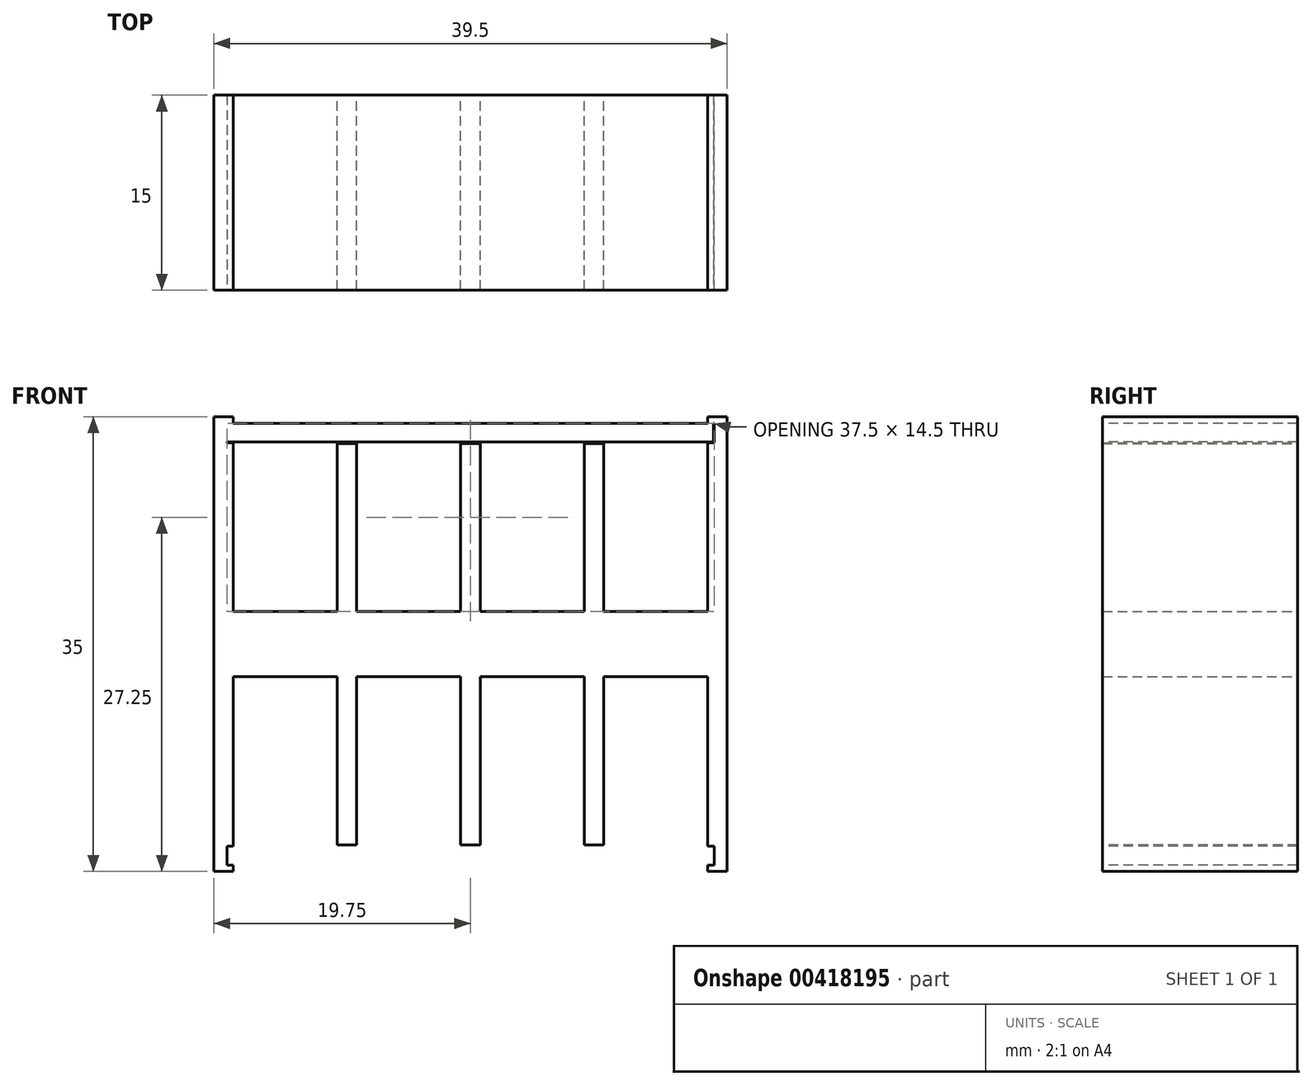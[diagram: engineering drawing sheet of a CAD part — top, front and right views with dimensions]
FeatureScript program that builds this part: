
annotation { "Feature Type Name" : "Feature", "Feature Type Description" : "" }
export const myFeature = defineFeature(function(context is Context, id is Id, definition is map)
    precondition{}
    {
        {
            var Q0;
            Q0=qCreatedBy(makeId("Top.planeOp"),FACE);
            var sketch = newSketch(context, id + "F0", { "sketchPlane" : qUnion([Q0])});
            skLineSegment(sketch, "E0.bottom", {"start": v(19.75, -7.5) * mm, "end": v(-19.75, -7.5) * mm});
            skLineSegment(sketch, "E0.top", {"start": v(19.75, 7.5) * mm, "end": v(-19.75, 7.5) * mm});
            skLineSegment(sketch, "E0.left", {"start": v(19.75, -7.5) * mm, "end": v(19.75, 7.5) * mm});
            skLineSegment(sketch, "E0.right", {"start": v(-19.75, -7.5) * mm, "end": v(-19.75, 7.5) * mm});
            skPoint(sketch, "E0.middle", {"position": v(0, 0) * mm});
            skSolve(sketch);
        }
        {
            var Q0;
            Q0=makeQuery(id+"F0.imprint","IMPRINT",FACE,{"disambiguationData":[TD([[makeQuery(id+"F0.imprint","IMPRINT",EDGE,{"derivedFrom":sQuery(id+"F0.wireOp",EDGE,"E0.bottom")}),-1.0]])]});
            extrude(context, id + "F1", {"entities" : qUnion([Q0]), "depth" : 5 * mm});
        }
        {
            var Q0;
            Q0=makeQuery(id+"F1.opExtrude","CAP_FACE",FACE,{"disambiguationData":[OSD([sQuery(id+"F0.wireOp",EDGE,"E0.bottom"),sQuery(id+"F0.wireOp",EDGE,"E0.top"),sQuery(id+"F0.wireOp",EDGE,"E0.left"),sQuery(id+"F0.wireOp",EDGE,"E0.right")])],"isStart":false});
            var sketch = newSketch(context, id + "F2", { "sketchPlane" : qUnion([Q0])});
            skLineSegment(sketch, "E1.bottom", {"start": v(-19.75, 7.5) * mm, "end": v(-18.25, 7.5) * mm});
            skLineSegment(sketch, "E1.top", {"start": v(-19.75, -7.5) * mm, "end": v(-18.25, -7.5) * mm});
            skLineSegment(sketch, "E1.left", {"start": v(-19.75, 7.5) * mm, "end": v(-19.75, -7.5) * mm});
            skLineSegment(sketch, "E1.right", {"start": v(-18.25, 7.5) * mm, "end": v(-18.25, -7.5) * mm});
            skLineSegment(sketch, "E2.bottom", {"start": v(19.75, 7.5) * mm, "end": v(18.25, 7.5) * mm});
            skLineSegment(sketch, "E2.top", {"start": v(19.75, -7.5) * mm, "end": v(18.25, -7.5) * mm});
            skLineSegment(sketch, "E2.left", {"start": v(19.75, 7.5) * mm, "end": v(19.75, -7.5) * mm});
            skLineSegment(sketch, "E2.right", {"start": v(18.25, 7.5) * mm, "end": v(18.25, -7.5) * mm});
            skLineSegment(sketch, "E3.bottom", {"start": v(0.75, -7.5) * mm, "end": v(-0.75, -7.5) * mm});
            skLineSegment(sketch, "E3.top", {"start": v(0.75, 7.5) * mm, "end": v(-0.75, 7.5) * mm});
            skLineSegment(sketch, "E3.left", {"start": v(0.75, -7.5) * mm, "end": v(0.75, 7.5) * mm});
            skLineSegment(sketch, "E3.right", {"start": v(-0.75, -7.5) * mm, "end": v(-0.75, 7.5) * mm});
            skPoint(sketch, "E3.middle", {"position": v(0, 0) * mm});
            skLineSegment(sketch, "E4.bottom", {"start": v(-18.25, 7.5) * mm, "end": v(-15.25, 7.5) * mm});
            skLineSegment(sketch, "E4.top", {"start": v(-18.25, -7.5) * mm, "end": v(-15.25, -7.5) * mm});
            skLineSegment(sketch, "E4.right", {"start": v(-15.25, 7.5) * mm, "end": v(-15.25, -7.5) * mm});
            skLineSegment(sketch, "E5.bottom", {"start": v(-0.75, 7.5) * mm, "end": v(-3.75, 7.5) * mm});
            skLineSegment(sketch, "E5.top", {"start": v(-0.75, -7.5) * mm, "end": v(-3.75, -7.5) * mm});
            skLineSegment(sketch, "E5.left", {"start": v(-0.75, 7.5) * mm, "end": v(-0.75, -7.5) * mm});
            skLineSegment(sketch, "E5.right", {"start": v(-3.75, 7.5) * mm, "end": v(-3.75, -7.5) * mm});
            skLineSegment(sketch, "E6.bottom", {"start": v(0.75, 7.5) * mm, "end": v(3.75, 7.5) * mm});
            skLineSegment(sketch, "E6.top", {"start": v(0.75, -7.5) * mm, "end": v(3.75, -7.5) * mm});
            skLineSegment(sketch, "E6.left", {"start": v(0.75, 7.5) * mm, "end": v(0.75, -7.5) * mm});
            skLineSegment(sketch, "E6.right", {"start": v(3.75, 7.5) * mm, "end": v(3.75, -7.5) * mm});
            skLineSegment(sketch, "E7.bottom", {"start": v(18.25, -7.5) * mm, "end": v(15.25, -7.5) * mm});
            skLineSegment(sketch, "E7.top", {"start": v(18.25, 7.5) * mm, "end": v(15.25, 7.5) * mm});
            skLineSegment(sketch, "E7.left", {"start": v(18.25, -7.5) * mm, "end": v(18.25, 7.5) * mm});
            skLineSegment(sketch, "E7.right", {"start": v(15.25, -7.5) * mm, "end": v(15.25, 7.5) * mm});
            skLineSegment(sketch, "E8.bottom", {"start": v(-15.25, 7.5) * mm, "end": v(-13.25, 7.5) * mm});
            skLineSegment(sketch, "E8.top", {"start": v(-15.25, -7.5) * mm, "end": v(-13.25, -7.5) * mm});
            skLineSegment(sketch, "E8.right", {"start": v(-13.25, 7.5) * mm, "end": v(-13.25, -7.5) * mm});
            skLineSegment(sketch, "E9.bottom", {"start": v(-3.75, -7.5) * mm, "end": v(-5.75, -7.5) * mm});
            skLineSegment(sketch, "E9.top", {"start": v(-3.75, 7.5) * mm, "end": v(-5.75, 7.5) * mm});
            skLineSegment(sketch, "E9.left", {"start": v(-3.75, -7.5) * mm, "end": v(-3.75, 7.5) * mm});
            skLineSegment(sketch, "E9.right", {"start": v(-5.75, -7.5) * mm, "end": v(-5.75, 7.5) * mm});
            skLineSegment(sketch, "E10.bottom", {"start": v(3.75, 7.5) * mm, "end": v(5.75, 7.5) * mm});
            skLineSegment(sketch, "E10.top", {"start": v(3.75, -7.5) * mm, "end": v(5.75, -7.5) * mm});
            skLineSegment(sketch, "E10.right", {"start": v(5.75, 7.5) * mm, "end": v(5.75, -7.5) * mm});
            skLineSegment(sketch, "E11.bottom", {"start": v(15.25, -7.5) * mm, "end": v(13.25, -7.5) * mm});
            skLineSegment(sketch, "E11.top", {"start": v(15.25, 7.5) * mm, "end": v(13.25, 7.5) * mm});
            skLineSegment(sketch, "E11.right", {"start": v(13.25, -7.5) * mm, "end": v(13.25, 7.5) * mm});
            skLineSegment(sketch, "E12.bottom", {"start": v(-13.25, 7.5) * mm, "end": v(-10.25, 7.5) * mm});
            skLineSegment(sketch, "E12.top", {"start": v(-13.25, -7.5) * mm, "end": v(-10.25, -7.5) * mm});
            skLineSegment(sketch, "E12.right", {"start": v(-10.25, 7.5) * mm, "end": v(-10.25, -7.5) * mm});
            skLineSegment(sketch, "E13.bottom", {"start": v(-5.75, -7.5) * mm, "end": v(-8.75, -7.5) * mm});
            skLineSegment(sketch, "E13.top", {"start": v(-5.75, 7.5) * mm, "end": v(-8.75, 7.5) * mm});
            skLineSegment(sketch, "E13.right", {"start": v(-8.75, -7.5) * mm, "end": v(-8.75, 7.5) * mm});
            skLineSegment(sketch, "E14.bottom", {"start": v(5.75, 7.5) * mm, "end": v(8.75, 7.5) * mm});
            skLineSegment(sketch, "E14.top", {"start": v(5.75, -7.5) * mm, "end": v(8.75, -7.5) * mm});
            skLineSegment(sketch, "E14.right", {"start": v(8.75, 7.5) * mm, "end": v(8.75, -7.5) * mm});
            skLineSegment(sketch, "E15.bottom", {"start": v(13.25, 7.5) * mm, "end": v(10.25, 7.5) * mm});
            skLineSegment(sketch, "E15.top", {"start": v(13.25, -7.5) * mm, "end": v(10.25, -7.5) * mm});
            skLineSegment(sketch, "E15.left", {"start": v(13.25, 7.5) * mm, "end": v(13.25, -7.5) * mm});
            skLineSegment(sketch, "E15.right", {"start": v(10.25, 7.5) * mm, "end": v(10.25, -7.5) * mm});
            skLineSegment(sketch, "E16.bottom", {"start": v(-10.25, -7.5) * mm, "end": v(-8.75, -7.5) * mm});
            skLineSegment(sketch, "E16.top", {"start": v(-10.25, 7.5) * mm, "end": v(-8.75, 7.5) * mm});
            skLineSegment(sketch, "E16.left", {"start": v(-10.25, -7.5) * mm, "end": v(-10.25, 7.5) * mm});
            skLineSegment(sketch, "E17.bottom", {"start": v(8.75, 7.5) * mm, "end": v(10.25, 7.5) * mm});
            skLineSegment(sketch, "E17.top", {"start": v(8.75, -7.5) * mm, "end": v(10.25, -7.5) * mm});
            skLineSegment(sketch, "E18", {"start": v(13.25, 0) * mm, "end": v(15.25, 0) * mm});
            skCircle(sketch, "E19", {"center": v(-14.25, 0) * mm, "radius": 1 * mm});
            skCircle(sketch, "E20", {"center": v(-4.75, 0) * mm, "radius": 1 * mm});
            skCircle(sketch, "E21", {"center": v(4.75, 0) * mm, "radius": 1 * mm});
            skCircle(sketch, "E22", {"center": v(14.25, 0) * mm, "radius": 1 * mm});
            skSolve(sketch);
        }
        {
            var Q0;
            Q0=makeQuery(id+"F2.imprint","IMPRINT",FACE,{"disambiguationData":[TD([[makeQuery(id+"F2.imprint","IMPRINT",EDGE,{"derivedFrom":sQuery(id+"F2.wireOp",EDGE,"E1.bottom")}),1.0]])]});
            var Q1;
            Q1=makeQuery(id+"F2.imprint","IMPRINT",FACE,{"disambiguationData":[TD([[makeQuery(id+"F2.imprint","IMPRINT",EDGE,{"derivedFrom":sQuery(id+"F2.wireOp",EDGE,"E16.bottom")}),-1.0]])]});
            var Q2;
            Q2=makeQuery(id+"F2.imprint","IMPRINT",FACE,{"disambiguationData":[TD([[makeQuery(id+"F2.imprint","IMPRINT",EDGE,{"derivedFrom":sQuery(id+"F2.wireOp",EDGE,"E3.bottom")}),-1.0]])]});
            var Q3;
            Q3=makeQuery(id+"F2.imprint","IMPRINT",FACE,{"disambiguationData":[TD([[makeQuery(id+"F2.imprint","IMPRINT",EDGE,{"derivedFrom":sQuery(id+"F2.wireOp",EDGE,"E17.bottom")}),1.0]])]});
            var Q4;
            Q4=makeQuery(id+"F2.imprint","IMPRINT",FACE,{"disambiguationData":[TD([[makeQuery(id+"F2.imprint","IMPRINT",EDGE,{"derivedFrom":sQuery(id+"F2.wireOp",EDGE,"E2.bottom")}),1.0]])]});
            extrude(context, id + "F3", {"entities" : qUnion([Q0, Q1, Q2, Q3, Q4]), "operationType" : NewBodyOperationType.ADD, "depth" : 15 * mm});
        }
        {
            var Q0;
            Q0=sQuery(id+"F2.wireOp",EDGE,"E19");
            var Q1;
            Q1=sQuery(id+"F2.wireOp",EDGE,"E20");
            var Q2;
            Q2=sQuery(id+"F2.wireOp",EDGE,"E21");
            var Q3;
            Q3=sQuery(id+"F2.wireOp",EDGE,"E22");
            extrude(context, id + "F4", {"bodyType" : ToolBodyType.SURFACE, "surfaceEntities" : qUnion([Q0, Q1, Q2, Q3]), "depth" : 12.95 * mm});
        }
        {
            var Q0;
            Q0=makeQuery(id+"F1.opExtrude","CAP_FACE",FACE,{"disambiguationData":[OSD([sQuery(id+"F0.wireOp",EDGE,"E0.bottom"),sQuery(id+"F0.wireOp",EDGE,"E0.top"),sQuery(id+"F0.wireOp",EDGE,"E0.left"),sQuery(id+"F0.wireOp",EDGE,"E0.right")])],"isStart":true});
            var sketch = newSketch(context, id + "F5", { "sketchPlane" : qUnion([Q0])});
            skLineSegment(sketch, "E23.bottom", {"start": v(0.75, -7.5) * mm, "end": v(-0.75, -7.5) * mm});
            skLineSegment(sketch, "E23.top", {"start": v(0.75, 7.5) * mm, "end": v(-0.75, 7.5) * mm});
            skLineSegment(sketch, "E23.left", {"start": v(0.75, -7.5) * mm, "end": v(0.75, 7.5) * mm});
            skLineSegment(sketch, "E23.right", {"start": v(-0.75, -7.5) * mm, "end": v(-0.75, 7.5) * mm});
            skPoint(sketch, "E23.middle", {"position": v(0, 0) * mm});
            skLineSegment(sketch, "E24.bottom", {"start": v(-19.75, 7.5) * mm, "end": v(-18.25, 7.5) * mm});
            skLineSegment(sketch, "E24.top", {"start": v(-19.75, -7.5) * mm, "end": v(-18.25, -7.5) * mm});
            skLineSegment(sketch, "E24.left", {"start": v(-19.75, 7.5) * mm, "end": v(-19.75, -7.5) * mm});
            skLineSegment(sketch, "E24.right", {"start": v(-18.25, 7.5) * mm, "end": v(-18.25, -7.5) * mm});
            skLineSegment(sketch, "E25.bottom", {"start": v(19.75, 7.5) * mm, "end": v(18.25, 7.5) * mm});
            skLineSegment(sketch, "E25.top", {"start": v(19.75, -7.5) * mm, "end": v(18.25, -7.5) * mm});
            skLineSegment(sketch, "E25.left", {"start": v(19.75, 7.5) * mm, "end": v(19.75, -7.5) * mm});
            skLineSegment(sketch, "E25.right", {"start": v(18.25, 7.5) * mm, "end": v(18.25, -7.5) * mm});
            skLineSegment(sketch, "E26.bottom", {"start": v(-18.25, 7.5) * mm, "end": v(-15.25, 7.5) * mm});
            skLineSegment(sketch, "E26.top", {"start": v(-18.25, -7.5) * mm, "end": v(-15.25, -7.5) * mm});
            skLineSegment(sketch, "E26.right", {"start": v(-15.25, 7.5) * mm, "end": v(-15.25, -7.5) * mm});
            skLineSegment(sketch, "E27.bottom", {"start": v(-0.75, 7.5) * mm, "end": v(-3.75, 7.5) * mm});
            skLineSegment(sketch, "E27.top", {"start": v(-0.75, -7.5) * mm, "end": v(-3.75, -7.5) * mm});
            skLineSegment(sketch, "E27.left", {"start": v(-0.75, 7.5) * mm, "end": v(-0.75, -7.5) * mm});
            skLineSegment(sketch, "E27.right", {"start": v(-3.75, 7.5) * mm, "end": v(-3.75, -7.5) * mm});
            skLineSegment(sketch, "E28.bottom", {"start": v(0.75, 7.5) * mm, "end": v(3.75, 7.5) * mm});
            skLineSegment(sketch, "E28.top", {"start": v(0.75, -7.5) * mm, "end": v(3.75, -7.5) * mm});
            skLineSegment(sketch, "E28.left", {"start": v(0.75, 7.5) * mm, "end": v(0.75, -7.5) * mm});
            skLineSegment(sketch, "E28.right", {"start": v(3.75, 7.5) * mm, "end": v(3.75, -7.5) * mm});
            skLineSegment(sketch, "E29.bottom", {"start": v(18.25, 7.5) * mm, "end": v(15.25, 7.5) * mm});
            skLineSegment(sketch, "E29.top", {"start": v(18.25, -7.5) * mm, "end": v(15.25, -7.5) * mm});
            skLineSegment(sketch, "E29.right", {"start": v(15.25, 7.5) * mm, "end": v(15.25, -7.5) * mm});
            skLineSegment(sketch, "E30.bottom", {"start": v(-15.25, 7.5) * mm, "end": v(-13.25, 7.5) * mm});
            skLineSegment(sketch, "E30.top", {"start": v(-15.25, -7.5) * mm, "end": v(-13.25, -7.5) * mm});
            skLineSegment(sketch, "E30.right", {"start": v(-13.25, 7.5) * mm, "end": v(-13.25, -7.5) * mm});
            skLineSegment(sketch, "E31.bottom", {"start": v(-3.75, 7.5) * mm, "end": v(-5.75, 7.5) * mm});
            skLineSegment(sketch, "E31.top", {"start": v(-3.75, -7.5) * mm, "end": v(-5.75, -7.5) * mm});
            skLineSegment(sketch, "E31.right", {"start": v(-5.75, 7.5) * mm, "end": v(-5.75, -7.5) * mm});
            skLineSegment(sketch, "E32.bottom", {"start": v(3.75, 7.5) * mm, "end": v(5.75, 7.5) * mm});
            skLineSegment(sketch, "E32.top", {"start": v(3.75, -7.5) * mm, "end": v(5.75, -7.5) * mm});
            skLineSegment(sketch, "E32.right", {"start": v(5.75, 7.5) * mm, "end": v(5.75, -7.5) * mm});
            skLineSegment(sketch, "E33.bottom", {"start": v(15.25, 7.5) * mm, "end": v(13.25, 7.5) * mm});
            skLineSegment(sketch, "E33.top", {"start": v(15.25, -7.5) * mm, "end": v(13.25, -7.5) * mm});
            skLineSegment(sketch, "E33.right", {"start": v(13.25, 7.5) * mm, "end": v(13.25, -7.5) * mm});
            skLineSegment(sketch, "E34.bottom", {"start": v(-13.25, 7.5) * mm, "end": v(-10.25, 7.5) * mm});
            skLineSegment(sketch, "E34.top", {"start": v(-13.25, -7.5) * mm, "end": v(-10.25, -7.5) * mm});
            skLineSegment(sketch, "E34.right", {"start": v(-10.25, 7.5) * mm, "end": v(-10.25, -7.5) * mm});
            skLineSegment(sketch, "E35.bottom", {"start": v(-5.75, 7.5) * mm, "end": v(-8.75, 7.5) * mm});
            skLineSegment(sketch, "E35.top", {"start": v(-5.75, -7.5) * mm, "end": v(-8.75, -7.5) * mm});
            skLineSegment(sketch, "E35.right", {"start": v(-8.75, 7.5) * mm, "end": v(-8.75, -7.5) * mm});
            skLineSegment(sketch, "E36.bottom", {"start": v(5.75, 7.5) * mm, "end": v(8.75, 7.5) * mm});
            skLineSegment(sketch, "E36.top", {"start": v(5.75, -7.5) * mm, "end": v(8.75, -7.5) * mm});
            skLineSegment(sketch, "E36.right", {"start": v(8.75, 7.5) * mm, "end": v(8.75, -7.5) * mm});
            skLineSegment(sketch, "E37.bottom", {"start": v(13.25, 7.5) * mm, "end": v(10.25, 7.5) * mm});
            skLineSegment(sketch, "E37.top", {"start": v(13.25, -7.5) * mm, "end": v(10.25, -7.5) * mm});
            skLineSegment(sketch, "E37.right", {"start": v(10.25, 7.5) * mm, "end": v(10.25, -7.5) * mm});
            skLineSegment(sketch, "E38.bottom", {"start": v(-10.25, 7.5) * mm, "end": v(-8.75, 7.5) * mm});
            skLineSegment(sketch, "E38.top", {"start": v(-10.25, -7.5) * mm, "end": v(-8.75, -7.5) * mm});
            skLineSegment(sketch, "E39.bottom", {"start": v(8.75, 7.5) * mm, "end": v(10.25, 7.5) * mm});
            skLineSegment(sketch, "E39.top", {"start": v(8.75, -7.5) * mm, "end": v(10.25, -7.5) * mm});
            skLineSegment(sketch, "E40", {"start": v(-15.25, 0) * mm, "end": v(-13.25, 0) * mm});
            skLineSegment(sketch, "E41", {"start": v(-5.75, 0) * mm, "end": v(-3.75, 0) * mm});
            skLineSegment(sketch, "E42", {"start": v(3.75, 0) * mm, "end": v(5.75, 0) * mm});
            skLineSegment(sketch, "E43", {"start": v(13.25, 0) * mm, "end": v(15.25, 0) * mm});
            skCircle(sketch, "E44", {"center": v(-14.25, 0) * mm, "radius": 1 * mm});
            skCircle(sketch, "E45", {"center": v(-4.75, 0) * mm, "radius": 1 * mm});
            skCircle(sketch, "E46", {"center": v(4.75, 0) * mm, "radius": 1 * mm});
            skCircle(sketch, "E47", {"center": v(14.25, 0) * mm, "radius": 1 * mm});
            skSolve(sketch);
        }
        {
            var Q0;
            Q0=makeQuery(id+"F5.imprint","IMPRINT",FACE,{"disambiguationData":[TD([[makeQuery(id+"F5.imprint","IMPRINT",EDGE,{"derivedFrom":sQuery(id+"F5.wireOp",EDGE,"E24.bottom")}),1.0]])]});
            var Q1;
            Q1=makeQuery(id+"F5.imprint","IMPRINT",FACE,{"disambiguationData":[TD([[makeQuery(id+"F5.imprint","IMPRINT",EDGE,{"derivedFrom":sQuery(id+"F5.wireOp",EDGE,"E25.bottom")}),1.0]])]});
            extrude(context, id + "F6", {"entities" : qUnion([Q0, Q1]), "operationType" : NewBodyOperationType.ADD, "depth" : 15 * mm});
        }
        {
            var Q0;
            Q0=makeQuery(id+"F5.imprint","IMPRINT",FACE,{"disambiguationData":[TD([[makeQuery(id+"F5.imprint","IMPRINT",EDGE,{"derivedFrom":sQuery(id+"F5.wireOp",EDGE,"E38.bottom")}),1.0]])]});
            var Q1;
            Q1=makeQuery(id+"F5.imprint","IMPRINT",FACE,{"disambiguationData":[TD([[makeQuery(id+"F5.imprint","IMPRINT",EDGE,{"derivedFrom":sQuery(id+"F5.wireOp",EDGE,"E23.bottom")}),-1.0]])]});
            var Q2;
            Q2=makeQuery(id+"F5.imprint","IMPRINT",FACE,{"disambiguationData":[TD([[makeQuery(id+"F5.imprint","IMPRINT",EDGE,{"derivedFrom":sQuery(id+"F5.wireOp",EDGE,"E39.bottom")}),1.0]])]});
            extrude(context, id + "F7", {"entities" : qUnion([Q0, Q1, Q2]), "operationType" : NewBodyOperationType.ADD, "depth" : 12.95 * mm});
        }
        {
            var Q0;
            Q0=sQuery(id+"F5.wireOp",EDGE,"E44");
            var Q1;
            Q1=sQuery(id+"F5.wireOp",EDGE,"E45");
            var Q2;
            Q2=sQuery(id+"F5.wireOp",EDGE,"E46");
            var Q3;
            Q3=sQuery(id+"F5.wireOp",EDGE,"E47");
            extrude(context, id + "F8", {"bodyType" : ToolBodyType.SURFACE, "surfaceEntities" : qUnion([Q0, Q1, Q2, Q3]), "depth" : 12.95 * mm});
        }
        {
            var Q0;
            Q0=makeQuery(id+"F7.boolean.opBoolean","MERGE",FACE,{"derivedFrom":[makeQuery(id+"F6.boolean.opBoolean","MERGE",FACE,{"derivedFrom":[makeQuery(id+"F3.boolean.opBoolean","MERGE",FACE,{"derivedFrom":[makeQuery(id+"F1.opExtrude","SWEPT_FACE",FACE,{"disambiguationData":[OSD([sQuery(id+"F0.wireOp",EDGE,"E0.top")])]}),makeQuery(id+"F3.opExtrude","SWEPT_FACE",FACE,{"disambiguationData":[OSD([sQuery(id+"F2.wireOp",EDGE,"E1.bottom")])]}),makeQuery(id+"F3.opExtrude","SWEPT_FACE",FACE,{"disambiguationData":[OSD([sQuery(id+"F2.wireOp",EDGE,"E2.bottom")])]}),makeQuery(id+"F3.opExtrude","SWEPT_FACE",FACE,{"disambiguationData":[OSD([sQuery(id+"F2.wireOp",EDGE,"E3.top")])]}),makeQuery(id+"F3.opExtrude","SWEPT_FACE",FACE,{"disambiguationData":[OSD([sQuery(id+"F2.wireOp",EDGE,"E16.top")])]}),makeQuery(id+"F3.opExtrude","SWEPT_FACE",FACE,{"disambiguationData":[OSD([sQuery(id+"F2.wireOp",EDGE,"E17.bottom")])]})]}),makeQuery(id+"F6.opExtrude","SWEPT_FACE",FACE,{"disambiguationData":[OSD([sQuery(id+"F5.wireOp",EDGE,"E24.top")])]}),makeQuery(id+"F6.opExtrude","SWEPT_FACE",FACE,{"disambiguationData":[OSD([sQuery(id+"F5.wireOp",EDGE,"E25.top")])]})]}),makeQuery(id+"F7.opExtrude","SWEPT_FACE",FACE,{"disambiguationData":[OSD([sQuery(id+"F5.wireOp",EDGE,"E23.bottom")])]}),makeQuery(id+"F7.opExtrude","SWEPT_FACE",FACE,{"disambiguationData":[OSD([sQuery(id+"F5.wireOp",EDGE,"E38.top")])]}),makeQuery(id+"F7.opExtrude","SWEPT_FACE",FACE,{"disambiguationData":[OSD([sQuery(id+"F5.wireOp",EDGE,"E39.top")])]})]});
            var sketch = newSketch(context, id + "F9", { "sketchPlane" : qUnion([Q0])});
            skLineSegment(sketch, "E48.bottom", {"start": v(-10.25, 20) * mm, "end": v(-8.75, 20) * mm});
            skLineSegment(sketch, "E48.top", {"start": v(-10.25, 17.95) * mm, "end": v(-8.75, 17.95) * mm});
            skLineSegment(sketch, "E48.left", {"start": v(-10.25, 20) * mm, "end": v(-10.25, 17.95) * mm});
            skLineSegment(sketch, "E48.right", {"start": v(-8.75, 20) * mm, "end": v(-8.75, 17.95) * mm});
            skLineSegment(sketch, "E49.bottom", {"start": v(-0.75, 20) * mm, "end": v(0.75, 20) * mm});
            skLineSegment(sketch, "E49.top", {"start": v(-0.75, 17.95) * mm, "end": v(0.75, 17.95) * mm});
            skLineSegment(sketch, "E49.left", {"start": v(-0.75, 20) * mm, "end": v(-0.75, 17.95) * mm});
            skLineSegment(sketch, "E49.right", {"start": v(0.75, 20) * mm, "end": v(0.75, 17.95) * mm});
            skLineSegment(sketch, "E50.bottom", {"start": v(8.75, 20) * mm, "end": v(10.25, 20) * mm});
            skLineSegment(sketch, "E50.top", {"start": v(8.75, 17.95) * mm, "end": v(10.25, 17.95) * mm});
            skLineSegment(sketch, "E50.left", {"start": v(8.75, 20) * mm, "end": v(8.75, 17.95) * mm});
            skLineSegment(sketch, "E50.right", {"start": v(10.25, 20) * mm, "end": v(10.25, 17.95) * mm});
            skLineSegment(sketch, "E51.bottom", {"start": v(18.25, 19.5) * mm, "end": v(18.75, 19.5) * mm});
            skLineSegment(sketch, "E51.top", {"start": v(18.25, 18) * mm, "end": v(18.75, 18) * mm});
            skLineSegment(sketch, "E51.left", {"start": v(18.25, 19.5) * mm, "end": v(18.25, 18) * mm});
            skLineSegment(sketch, "E51.right", {"start": v(18.75, 19.5) * mm, "end": v(18.75, 18) * mm});
            skLineSegment(sketch, "E52.bottom", {"start": v(-18.25, 19.5) * mm, "end": v(-18.75, 19.5) * mm});
            skLineSegment(sketch, "E52.top", {"start": v(-18.25, 18) * mm, "end": v(-18.75, 18) * mm});
            skLineSegment(sketch, "E52.left", {"start": v(-18.25, 19.5) * mm, "end": v(-18.25, 18) * mm});
            skLineSegment(sketch, "E52.right", {"start": v(-18.75, 19.5) * mm, "end": v(-18.75, 18) * mm});
            skSolve(sketch);
        }
        {
            var Q0;
            Q0=makeQuery(id+"F9.imprint","IMPRINT",FACE,{"disambiguationData":[TD([[makeQuery(id+"F9.imprint","IMPRINT",EDGE,{"derivedFrom":sQuery(id+"F9.wireOp",EDGE,"E51.bottom")}),-1.0]])]});
            var Q1;
            Q1=makeQuery(id+"F9.imprint","IMPRINT",FACE,{"disambiguationData":[TD([[makeQuery(id+"F9.imprint","IMPRINT",EDGE,{"derivedFrom":sQuery(id+"F9.wireOp",EDGE,"E52.bottom")}),1.0]])]});
            extrude(context, id + "F10", {"entities" : qUnion([Q0, Q1]), "operationType" : NewBodyOperationType.REMOVE, "oppositeDirection" : true, "depth" : 15 * mm});
        }
        {
            var Q0;
            Q0=makeQuery(id+"F9.imprint","IMPRINT",FACE,{"disambiguationData":[TD([[makeQuery(id+"F9.imprint","IMPRINT",EDGE,{"derivedFrom":sQuery(id+"F9.wireOp",EDGE,"E48.bottom")}),-1.0]])]});
            var Q1;
            Q1=makeQuery(id+"F9.imprint","IMPRINT",FACE,{"disambiguationData":[TD([[makeQuery(id+"F9.imprint","IMPRINT",EDGE,{"derivedFrom":sQuery(id+"F9.wireOp",EDGE,"E49.bottom")}),-1.0]])]});
            var Q2;
            Q2=makeQuery(id+"F9.imprint","IMPRINT",FACE,{"disambiguationData":[TD([[makeQuery(id+"F9.imprint","IMPRINT",EDGE,{"derivedFrom":sQuery(id+"F9.wireOp",EDGE,"E50.bottom")}),-1.0]])]});
            extrude(context, id + "F11", {"entities" : qUnion([Q0, Q1, Q2]), "operationType" : NewBodyOperationType.REMOVE, "oppositeDirection" : true, "depth" : 15 * mm});
        }
        {
            var Q0;
            Q0=makeQuery(id+"F7.boolean.opBoolean","MERGE",FACE,{"derivedFrom":[makeQuery(id+"F6.boolean.opBoolean","MERGE",FACE,{"derivedFrom":[makeQuery(id+"F3.boolean.opBoolean","MERGE",FACE,{"derivedFrom":[makeQuery(id+"F1.opExtrude","SWEPT_FACE",FACE,{"disambiguationData":[OSD([sQuery(id+"F0.wireOp",EDGE,"E0.bottom")])]}),makeQuery(id+"F3.opExtrude","SWEPT_FACE",FACE,{"disambiguationData":[OSD([sQuery(id+"F2.wireOp",EDGE,"E1.top")])]}),makeQuery(id+"F3.opExtrude","SWEPT_FACE",FACE,{"disambiguationData":[OSD([sQuery(id+"F2.wireOp",EDGE,"E2.top")])]}),makeQuery(id+"F3.opExtrude","SWEPT_FACE",FACE,{"disambiguationData":[OSD([sQuery(id+"F2.wireOp",EDGE,"E3.bottom")])]}),makeQuery(id+"F3.opExtrude","SWEPT_FACE",FACE,{"disambiguationData":[OSD([sQuery(id+"F2.wireOp",EDGE,"E16.bottom")])]}),makeQuery(id+"F3.opExtrude","SWEPT_FACE",FACE,{"disambiguationData":[OSD([sQuery(id+"F2.wireOp",EDGE,"E17.top")])]})]}),makeQuery(id+"F6.opExtrude","SWEPT_FACE",FACE,{"disambiguationData":[OSD([sQuery(id+"F5.wireOp",EDGE,"E24.bottom")])]}),makeQuery(id+"F6.opExtrude","SWEPT_FACE",FACE,{"disambiguationData":[OSD([sQuery(id+"F5.wireOp",EDGE,"E25.bottom")])]})]}),makeQuery(id+"F7.opExtrude","SWEPT_FACE",FACE,{"disambiguationData":[OSD([sQuery(id+"F5.wireOp",EDGE,"E23.top")])]}),makeQuery(id+"F7.opExtrude","SWEPT_FACE",FACE,{"disambiguationData":[OSD([sQuery(id+"F5.wireOp",EDGE,"E38.bottom")])]}),makeQuery(id+"F7.opExtrude","SWEPT_FACE",FACE,{"disambiguationData":[OSD([sQuery(id+"F5.wireOp",EDGE,"E39.bottom")])]})]});
            var sketch = newSketch(context, id + "F12", { "sketchPlane" : qUnion([Q0])});
            skLineSegment(sketch, "E53.bottom", {"start": v(-18.75, 19.5) * mm, "end": v(18.7, 19.5) * mm});
            skLineSegment(sketch, "E53.top", {"start": v(-18.75, 18.05) * mm, "end": v(18.7, 18.05) * mm});
            skLineSegment(sketch, "E53.left", {"start": v(-18.75, 19.5) * mm, "end": v(-18.75, 18.05) * mm});
            skLineSegment(sketch, "E53.right", {"start": v(18.7, 19.5) * mm, "end": v(18.7, 18.05) * mm});
            skSolve(sketch);
        }
        {
            var Q0;
            Q0=makeQuery(id+"F12.imprint","IMPRINT",FACE,{"disambiguationData":[TD([[makeQuery(id+"F12.imprint","IMPRINT",EDGE,{"derivedFrom":sQuery(id+"F12.wireOp",EDGE,"E53.top")}),1.0]])]});
            extrude(context, id + "F13", {"entities" : qUnion([Q0]), "operationType" : NewBodyOperationType.ADD, "oppositeDirection" : true, "depth" : 15 * mm});
        }
        {
            var Q0;
            Q0=makeQuery(id+"F13.boolean.opBoolean","MERGE",FACE,{"derivedFrom":[makeQuery(id+"F7.boolean.opBoolean","MERGE",FACE,{"derivedFrom":[makeQuery(id+"F6.boolean.opBoolean","MERGE",FACE,{"derivedFrom":[makeQuery(id+"F3.boolean.opBoolean","MERGE",FACE,{"derivedFrom":[makeQuery(id+"F1.opExtrude","SWEPT_FACE",FACE,{"disambiguationData":[OSD([sQuery(id+"F0.wireOp",EDGE,"E0.bottom")])]}),makeQuery(id+"F3.opExtrude","SWEPT_FACE",FACE,{"disambiguationData":[OSD([sQuery(id+"F2.wireOp",EDGE,"E1.top")])]}),makeQuery(id+"F3.opExtrude","SWEPT_FACE",FACE,{"disambiguationData":[OSD([sQuery(id+"F2.wireOp",EDGE,"E2.top")])]}),makeQuery(id+"F3.opExtrude","SWEPT_FACE",FACE,{"disambiguationData":[OSD([sQuery(id+"F2.wireOp",EDGE,"E3.bottom")])]}),makeQuery(id+"F3.opExtrude","SWEPT_FACE",FACE,{"disambiguationData":[OSD([sQuery(id+"F2.wireOp",EDGE,"E16.bottom")])]}),makeQuery(id+"F3.opExtrude","SWEPT_FACE",FACE,{"disambiguationData":[OSD([sQuery(id+"F2.wireOp",EDGE,"E17.top")])]})]}),makeQuery(id+"F6.opExtrude","SWEPT_FACE",FACE,{"disambiguationData":[OSD([sQuery(id+"F5.wireOp",EDGE,"E24.bottom")])]}),makeQuery(id+"F6.opExtrude","SWEPT_FACE",FACE,{"disambiguationData":[OSD([sQuery(id+"F5.wireOp",EDGE,"E25.bottom")])]})]}),makeQuery(id+"F7.opExtrude","SWEPT_FACE",FACE,{"disambiguationData":[OSD([sQuery(id+"F5.wireOp",EDGE,"E23.top")])]}),makeQuery(id+"F7.opExtrude","SWEPT_FACE",FACE,{"disambiguationData":[OSD([sQuery(id+"F5.wireOp",EDGE,"E38.bottom")])]}),makeQuery(id+"F7.opExtrude","SWEPT_FACE",FACE,{"disambiguationData":[OSD([sQuery(id+"F5.wireOp",EDGE,"E39.bottom")])]})]}),makeQuery(id+"F13.opExtrude","CAP_FACE",FACE,{"disambiguationData":[OSD([sQuery(id+"F12.wireOp",EDGE,"E53.bottom"),sQuery(id+"F12.wireOp",EDGE,"E53.top"),sQuery(id+"F12.wireOp",EDGE,"E53.left"),sQuery(id+"F12.wireOp",EDGE,"E53.right")])],"isStart":true})]});
            var sketch = newSketch(context, id + "F14", { "sketchPlane" : qUnion([Q0])});
            skLineSegment(sketch, "E54.bottom", {"start": v(-18.25, -14.5) * mm, "end": v(-18.75, -14.5) * mm});
            skLineSegment(sketch, "E54.top", {"start": v(-18.25, -13.05) * mm, "end": v(-18.75, -13.05) * mm});
            skLineSegment(sketch, "E54.left", {"start": v(-18.25, -14.5) * mm, "end": v(-18.25, -13.05) * mm});
            skLineSegment(sketch, "E54.right", {"start": v(-18.75, -14.5) * mm, "end": v(-18.75, -13.05) * mm});
            skPoint(sketch, "E55.oppositeSnap0", {"position": v(19, -15) * mm});
            skLineSegment(sketch, "E56.bottom", {"start": v(18.25, -14.5) * mm, "end": v(18.75, -14.5) * mm});
            skLineSegment(sketch, "E56.top", {"start": v(18.25, -13.05) * mm, "end": v(18.75, -13.05) * mm});
            skLineSegment(sketch, "E56.left", {"start": v(18.25, -14.5) * mm, "end": v(18.25, -13.05) * mm});
            skLineSegment(sketch, "E56.right", {"start": v(18.75, -14.5) * mm, "end": v(18.75, -13.05) * mm});
            skSolve(sketch);
        }
        {
            var Q0;
            Q0=makeQuery(id+"F14.imprint","IMPRINT",FACE,{"disambiguationData":[TD([[makeQuery(id+"F14.imprint","IMPRINT",EDGE,{"derivedFrom":sQuery(id+"F14.wireOp",EDGE,"E56.bottom")}),1.0]])]});
            var Q1;
            Q1=makeQuery(id+"F14.imprint","IMPRINT",FACE,{"disambiguationData":[TD([[makeQuery(id+"F14.imprint","IMPRINT",EDGE,{"derivedFrom":sQuery(id+"F14.wireOp",EDGE,"E54.bottom")}),-1.0]])]});
            extrude(context, id + "F15", {"entities" : qUnion([Q0, Q1]), "operationType" : NewBodyOperationType.REMOVE, "oppositeDirection" : true, "depth" : 15 * mm});
        }
    });
